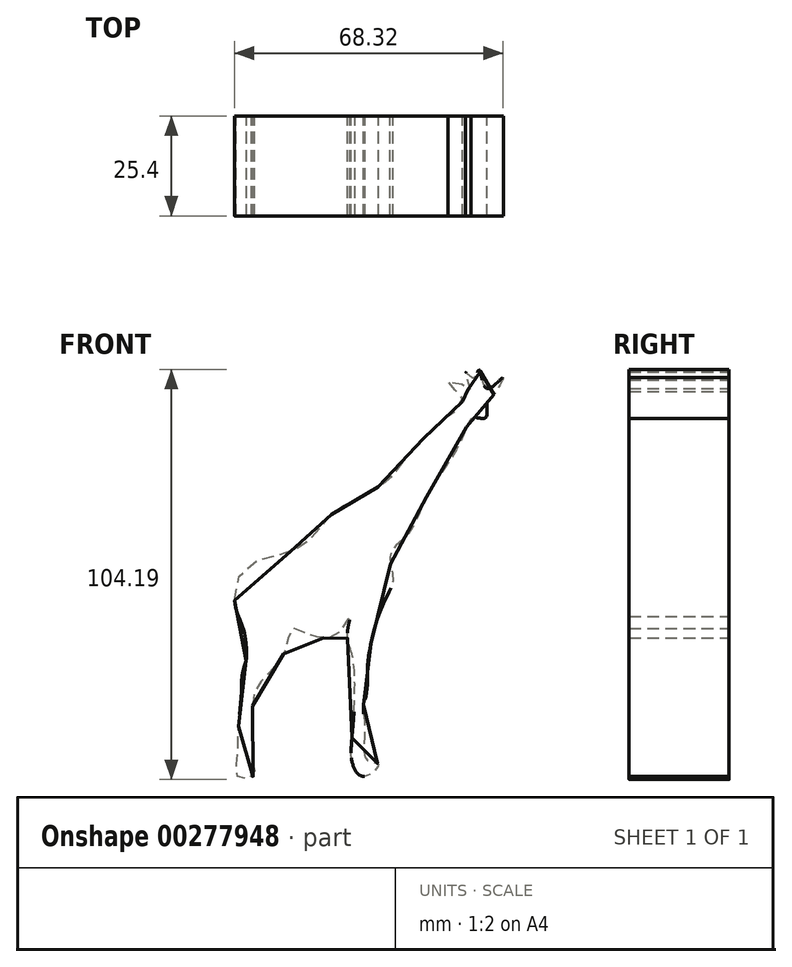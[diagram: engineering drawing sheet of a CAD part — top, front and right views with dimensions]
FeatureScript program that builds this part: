
annotation { "Feature Type Name" : "Feature", "Feature Type Description" : "" }
export const myFeature = defineFeature(function(context is Context, id is Id, definition is map)
    precondition{}
    {
        {
            var Q0;
            Q0=qCreatedBy(makeId("Front.planeOp"),FACE);
            var sketch = newSketch(context, id + "F0", { "sketchPlane" : qUnion([Q0])});
            skFitSpline(sketch, "E0", {"points": [v(-10.24, -19.62) * mm, v(-6.82, -10.75) * mm, v(2.39, -7.68) * mm, v(6.82, -5.63) * mm, v(10.58, -2.56) * mm, v(12.28, 0) * mm, v(16.04, 3.58) * mm, v(19.79, 5.63) * mm, v(22.86, 7) * mm, v(25.93, 9.04) * mm, v(29.34, 11.43) * mm, v(32.07, 14.84) * mm, v(37.87, 21.67) * mm, v(41.63, 25.08) * mm, v(44.36, 27.8) * mm, v(47.08, 29.51) * mm, v(47.43, 32.93) * mm, v(45.04, 34.3) * mm, v(44.01, 36) * mm, v(47.08, 35.65) * mm, v(49.81, 33.6) * mm, v(48.45, 38.38) * mm, v(50.5, 37.02) * mm, v(51.86, 39.07) * mm, v(52.89, 35.65) * mm, v(54.6, 34.3) * mm, v(58, 37.02) * mm, v(55.27, 32.24) * mm, v(53.9, 30.54) * mm, v(53.57, 26.78) * mm, v(50.5, 26.78) * mm, v(47.77, 22) * mm, v(43, 13.82) * mm, v(38.55, 6.65) * mm, v(33.44, -3.24) * mm, v(29.34, -7.68) * mm, v(30.03, -14.16) * mm, v(27.64, -20.3) * mm, v(23.88, -33.27) * mm, v(23.54, -38.73) * mm, v(23.2, -43.84) * mm, v(22.52, -46.57) * mm, v(22.86, -52.37) * mm, v(23.54, -60.22) * mm, v(26.27, -61.24) * mm, v(22.86, -64.32) * mm, v(19.79, -61.24) * mm, v(19.79, -52.37) * mm, v(19.79, -33.95) * mm, v(18.42, -28.15) * mm, v(19.1, -23.71) * mm, v(16.38, -27.8) * mm, v(12.62, -29.17) * mm, v(7.5, -27.8) * mm, v(4.44, -26.78) * mm, v(2.73, -31.9) * mm, v(0, -36.34) * mm, v(-3.07, -39.75) * mm, v(-5.46, -43.84) * mm, v(-5.46, -55.1) * mm, v(-5.8, -59.88) * mm, v(-5.46, -64.32) * mm, v(-9.21, -64.66) * mm, v(-9.55, -59.88) * mm, v(-9.21, -51.35) * mm, v(-8.53, -44.18) * mm, v(-8.19, -38.04) * mm, v(-7.17, -33.95) * mm, v(-7.5, -29.17) * mm, v(-7.85, -27.12) * mm, v(-10.24, -19.62) * mm]});
            skSolve(sketch);
        }
        {
            var Q0;
            Q0 = qSketchRegion(id + "F0", true);
            extrude(context, id + "F1", {"entities" : qUnion([Q0]), "depth" : 25.4 * mm});
        }
    });
